# Revit family: Domotics-DomesticRanges-GEWISS-27COMBI_SYSTEM-IP40_SOCKET-OUTLET_ITA
name_source: partatom
category: Apparecchi elettrici
revit_build: Autodesk Revit 2016 (Build: 20161004_0715(x64)
units: mm (PartAtom-declared; Revit-internal decimal feet)

## family parameters
Condiviso = Sì
Host = Superficie
Mantenere orientamento annotazione = Sì
Numero OmniClass = 23.80.50.14
Punto di calcolo locali = No
Quota connettore circolare = Usa diametro
Taglio con vuoti quando caricato = Sì
Tipo di parte = Normale
Titolo OmniClass = Plug Connectors

## types (1)
- Domotics-DomesticRanges-GEWISS-27COMBI_SYSTEM-IP40_SOCKET-OUTLET_ITA
    Bidimensionale = bidimensionale system contenitori IP40 : 2P
    Catalogue = DOMOTICS
    Catalogue Range = 27COMBI
    Characteristics = Italian standard
    Colour = Grey RAL 7035
    Description: = S.-outlet 2P+E - 16A Dual amp
    Descrizione = 2P+E 16A DUAL AMP ITA STD SOCKET IP40
    Dimensions LxHxD (mm) = 66x82x55
    EAN code = 8011564095397
    Electrocod = 0131
    GW - Testo elettrico = 10/16
    Glow Wire Test = 650°C
    IDF = a4afe3af-0453-46d6-b7ae-c7b1faa88fc2
    IDT = 064142aa-a4a2-459b-b726-830832a9daec
    IP degree = IP40
    Immagine tipo = GW27811.jpg
    Installation temperature = -25 +60 °C
    Insulation class = II
    Larghezza foro = 23 mm  [stored 0.0754593 ft]
    Larghezza scatola = 66 mm  [stored 0.216535 ft]
    Lid screws = Corrosion-resistant steel
    Modello = GW27811
    N. holes Ã˜ 23 with cable gland = 1
    No. knockout holes Ã˜23 = 3 on sides / 1 on the bottom
    Outer dim. LxHxD (mm) = 66x82x55
    Produttore = GEWISS S.p.A.
    Prospetto di default = 1219 mm
    SCATOLA = GEWISS GRIGIO
    SEO = Enclosure
    Simbolo = SIMBOLO PRESE : PRESA
    Standard; = IEC 60884-1
    Technical sheet = https://www.gewiss.com
    Thermo-pressure with ball = 70
    Torque screws tightening = 0,8NM
    Type of knockout holes = Removable with tool
    URL = https://www.gewiss.com
    Version file RFA = 19.4
    Voltage = 230V ac
    Voltage: = 250 V ac

note: source unit labels omitted for Thermo-pressure with ball — the stored unit's dimension contradicts the parameter name (converter mislabeling)

note: [stored X ft] marks values corroborated as IEEE doubles in the binary element streams (Revit-internal decimal feet)

## geometry (parser evidence)
native form markers: Sweep x1
no freeform markers — native parametric forms only
